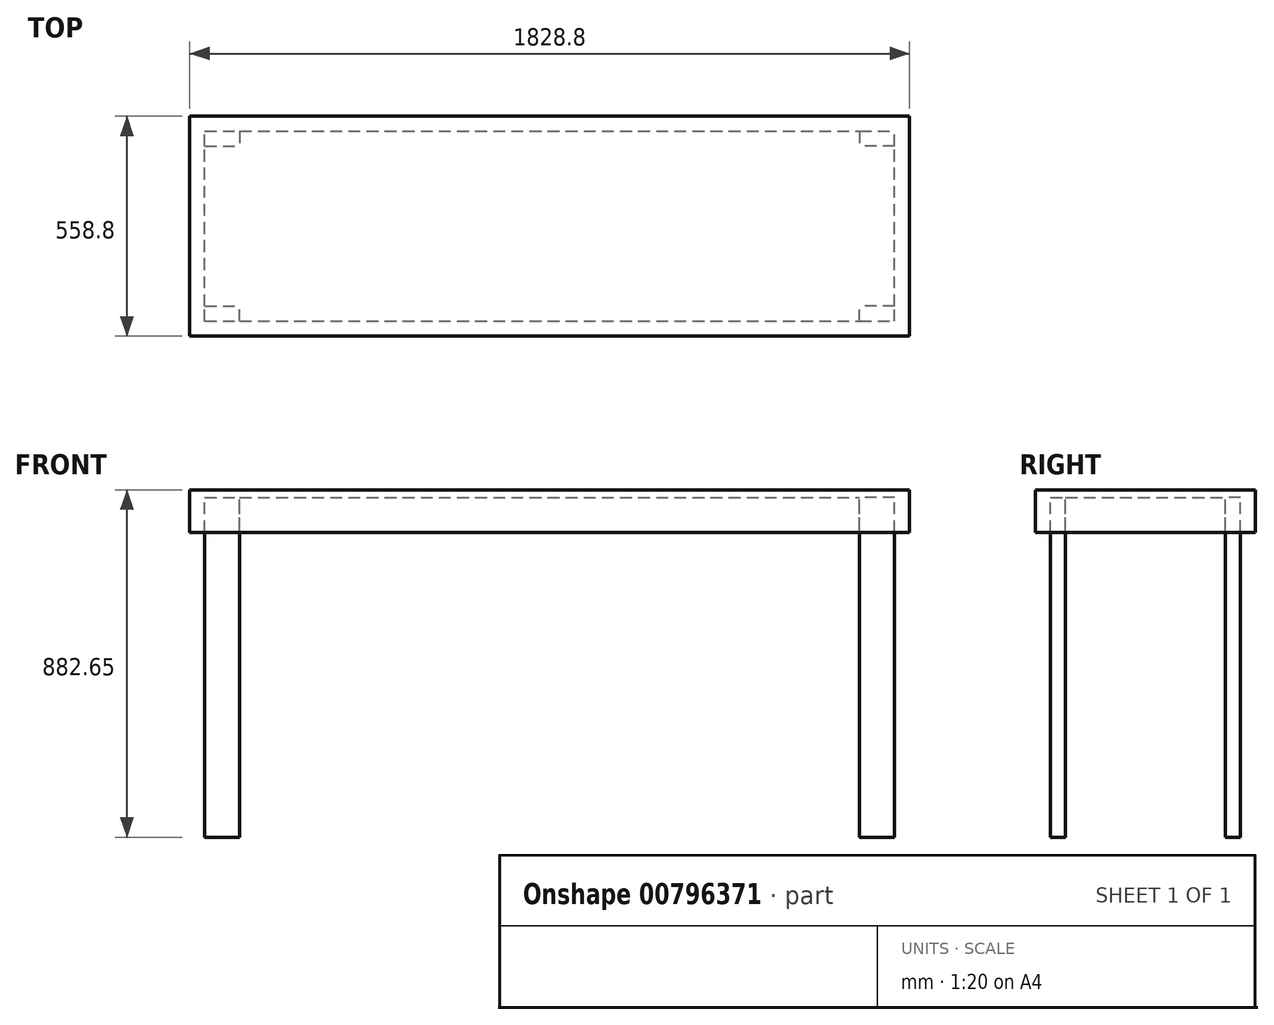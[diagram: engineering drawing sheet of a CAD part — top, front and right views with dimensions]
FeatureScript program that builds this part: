
annotation { "Feature Type Name" : "Feature", "Feature Type Description" : "" }
export const myFeature = defineFeature(function(context is Context, id is Id, definition is map)
    precondition{}
    {
        {
            var Q0;
            Q0=qCreatedBy(makeId("Top.planeOp"),FACE);
            var sketch = newSketch(context, id + "F0", { "sketchPlane" : qUnion([Q0])});
            skLineSegment(sketch, "E0.bottom", {"start": v(0, 0) * mm, "end": v(1828.8, 0) * mm});
            skLineSegment(sketch, "E0.top", {"start": v(0, -558.8) * mm, "end": v(1828.8, -558.8) * mm});
            skLineSegment(sketch, "E0.left", {"start": v(0, 0) * mm, "end": v(0, -558.8) * mm});
            skLineSegment(sketch, "E0.right", {"start": v(1828.8, 0) * mm, "end": v(1828.8, -558.8) * mm});
            skSolve(sketch);
        }
        {
            var Q0;
            Q0=makeQuery(id+"F0.imprint","IMPRINT",FACE,{"disambiguationData":[TD([[makeQuery(id+"F0.imprint","IMPRINT",EDGE,{"derivedFrom":sQuery(id+"F0.wireOp",EDGE,"E0.bottom")}),-1.0]])]});
            extrude(context, id + "F1", {"entities" : qUnion([Q0]), "depth" : 19.05 * mm, "offsetDistance" : 25.4 * mm});
        }
        {
            var Q0;
            Q0=makeQuery(id+"F1.opExtrude","SWEPT_FACE",FACE,{"disambiguationData":[OSD([sQuery(id+"F0.wireOp",EDGE,"E0.right")])]});
            var sketch = newSketch(context, id + "F2", { "sketchPlane" : qUnion([Q0])});
            skLineSegment(sketch, "E1.bottom", {"start": v(-558.8, 0) * mm, "end": v(-520.7, 0) * mm});
            skLineSegment(sketch, "E1.top", {"start": v(-558.8, -88.9) * mm, "end": v(-520.7, -88.9) * mm});
            skLineSegment(sketch, "E1.left", {"start": v(-558.8, 0) * mm, "end": v(-558.8, -88.9) * mm});
            skLineSegment(sketch, "E1.right", {"start": v(-520.7, 0) * mm, "end": v(-520.7, -88.9) * mm});
            skLineSegment(sketch, "E2.bottom", {"start": v(0, 0) * mm, "end": v(-38.1, 0) * mm});
            skLineSegment(sketch, "E2.top", {"start": v(0, -88.9) * mm, "end": v(-38.1, -88.9) * mm});
            skLineSegment(sketch, "E2.left", {"start": v(0, 0) * mm, "end": v(0, -88.9) * mm});
            skLineSegment(sketch, "E2.right", {"start": v(-38.1, 0) * mm, "end": v(-38.1, -88.9) * mm});
            skSolve(sketch);
        }
        {
            var Q0;
            Q0 = qSketchRegion(id + "F2", true);
            var Q1;
            Q1=makeQuery(id+"F1.opExtrude","SWEPT_FACE",FACE,{"disambiguationData":[OSD([sQuery(id+"F0.wireOp",EDGE,"E0.left")])]});
            extrude(context, id + "F3", {"entities" : qUnion([Q0]), "operationType" : NewBodyOperationType.ADD, "endBound" : BoundingType.UP_TO_SURFACE, "oppositeDirection" : true, "depth" : 25.4 * mm, "endBoundEntityFace" : qUnion([Q1]), "offsetDistance" : 25.4 * mm});
        }
        {
            var Q0;
            Q0=makeQuery(id+"F3.opExtrude","SWEPT_FACE",FACE,{"disambiguationData":[OSD([sQuery(id+"F2.wireOp",EDGE,"E2.right")])]});
            var sketch = newSketch(context, id + "F4", { "sketchPlane" : qUnion([Q0])});
            skLineSegment(sketch, "E3.bottom", {"start": v(0, 0) * mm, "end": v(38.1, 0) * mm});
            skLineSegment(sketch, "E3.top", {"start": v(0, -88.9) * mm, "end": v(38.1, -88.9) * mm});
            skLineSegment(sketch, "E3.left", {"start": v(0, 0) * mm, "end": v(0, -88.9) * mm});
            skLineSegment(sketch, "E3.right", {"start": v(38.1, 0) * mm, "end": v(38.1, -88.9) * mm});
            skLineSegment(sketch, "E4.bottom", {"start": v(1828.8, 0) * mm, "end": v(1790.7, 0) * mm});
            skLineSegment(sketch, "E4.top", {"start": v(1828.8, -88.9) * mm, "end": v(1790.7, -88.9) * mm});
            skLineSegment(sketch, "E4.left", {"start": v(1828.8, 0) * mm, "end": v(1828.8, -88.9) * mm});
            skLineSegment(sketch, "E4.right", {"start": v(1790.7, 0) * mm, "end": v(1790.7, -88.9) * mm});
            skSolve(sketch);
        }
        {
            var Q0;
            Q0=makeQuery(id+"F4.imprint","IMPRINT",FACE,{"disambiguationData":[TD([[makeQuery(id+"F4.imprint","IMPRINT",EDGE,{"derivedFrom":sQuery(id+"F4.wireOp",EDGE,"E3.bottom")}),-1.0]])]});
            var Q1;
            Q1=makeQuery(id+"F4.imprint","IMPRINT",FACE,{"disambiguationData":[TD([[makeQuery(id+"F4.imprint","IMPRINT",EDGE,{"derivedFrom":sQuery(id+"F4.wireOp",EDGE,"E4.bottom")}),-1.0]])]});
            extrude(context, id + "F5", {"entities" : qUnion([Q0, Q1]), "operationType" : NewBodyOperationType.ADD, "endBound" : BoundingType.UP_TO_NEXT, "depth" : 25.4 * mm, "offsetDistance" : 25.4 * mm});
        }
        {
            var Q0;
            Q0=makeQuery(id+"F1.opExtrude","CAP_FACE",FACE,{"disambiguationData":[OSD([sQuery(id+"F0.wireOp",EDGE,"E0.bottom"),sQuery(id+"F0.wireOp",EDGE,"E0.top"),sQuery(id+"F0.wireOp",EDGE,"E0.left"),sQuery(id+"F0.wireOp",EDGE,"E0.right")])],"isStart":true});
            var sketch = newSketch(context, id + "F6", { "sketchPlane" : qUnion([Q0])});
            skLineSegment(sketch, "E5.bottom", {"start": v(38.1, 520.7) * mm, "end": v(127, 520.7) * mm});
            skLineSegment(sketch, "E5.top", {"start": v(38.1, 482.6) * mm, "end": v(127, 482.6) * mm});
            skLineSegment(sketch, "E5.left", {"start": v(38.1, 520.7) * mm, "end": v(38.1, 482.6) * mm});
            skLineSegment(sketch, "E5.right", {"start": v(127, 520.7) * mm, "end": v(127, 482.6) * mm});
            skLineSegment(sketch, "E6.bottom", {"start": v(1790.7, 520.7) * mm, "end": v(1701.8, 520.7) * mm});
            skLineSegment(sketch, "E6.top", {"start": v(1790.7, 482.6) * mm, "end": v(1701.8, 482.6) * mm});
            skLineSegment(sketch, "E6.left", {"start": v(1790.7, 520.7) * mm, "end": v(1790.7, 482.6) * mm});
            skLineSegment(sketch, "E6.right", {"start": v(1701.8, 520.7) * mm, "end": v(1701.8, 482.6) * mm});
            skLineSegment(sketch, "E7.bottom", {"start": v(1790.7, 38.1) * mm, "end": v(1701.8, 38.1) * mm});
            skLineSegment(sketch, "E7.top", {"start": v(1790.7, 76.2) * mm, "end": v(1701.8, 76.2) * mm});
            skLineSegment(sketch, "E7.left", {"start": v(1790.7, 38.1) * mm, "end": v(1790.7, 76.2) * mm});
            skLineSegment(sketch, "E7.right", {"start": v(1701.8, 38.1) * mm, "end": v(1701.8, 76.2) * mm});
            skLineSegment(sketch, "E8.bottom", {"start": v(38.1, 38.1) * mm, "end": v(127, 38.1) * mm});
            skLineSegment(sketch, "E8.top", {"start": v(38.1, 76.2) * mm, "end": v(127, 76.2) * mm});
            skLineSegment(sketch, "E8.left", {"start": v(38.1, 38.1) * mm, "end": v(38.1, 76.2) * mm});
            skLineSegment(sketch, "E8.right", {"start": v(127, 38.1) * mm, "end": v(127, 76.2) * mm});
            skSolve(sketch);
        }
        {
            var Q0;
            Q0=makeQuery(id+"F6.imprint","IMPRINT",FACE,{"disambiguationData":[TD([[makeQuery(id+"F6.imprint","IMPRINT",EDGE,{"derivedFrom":sQuery(id+"F6.wireOp",EDGE,"E6.bottom")}),-1.0]])]});
            var Q1;
            Q1=makeQuery(id+"F6.imprint","IMPRINT",FACE,{"disambiguationData":[TD([[makeQuery(id+"F6.imprint","IMPRINT",EDGE,{"derivedFrom":sQuery(id+"F6.wireOp",EDGE,"E7.bottom")}),1.0]])]});
            var Q2;
            Q2=makeQuery(id+"F6.imprint","IMPRINT",FACE,{"disambiguationData":[TD([[makeQuery(id+"F6.imprint","IMPRINT",EDGE,{"derivedFrom":sQuery(id+"F6.wireOp",EDGE,"E8.bottom")}),1.0]])]});
            var Q3;
            Q3=makeQuery(id+"F6.imprint","IMPRINT",FACE,{"disambiguationData":[TD([[makeQuery(id+"F6.imprint","IMPRINT",EDGE,{"derivedFrom":sQuery(id+"F6.wireOp",EDGE,"E5.bottom")}),-1.0]])]});
            extrude(context, id + "F7", {"entities" : qUnion([Q0, Q1, Q2, Q3]), "operationType" : NewBodyOperationType.ADD, "depth" : 863.6 * mm, "offsetDistance" : 25.4 * mm});
        }
    });
